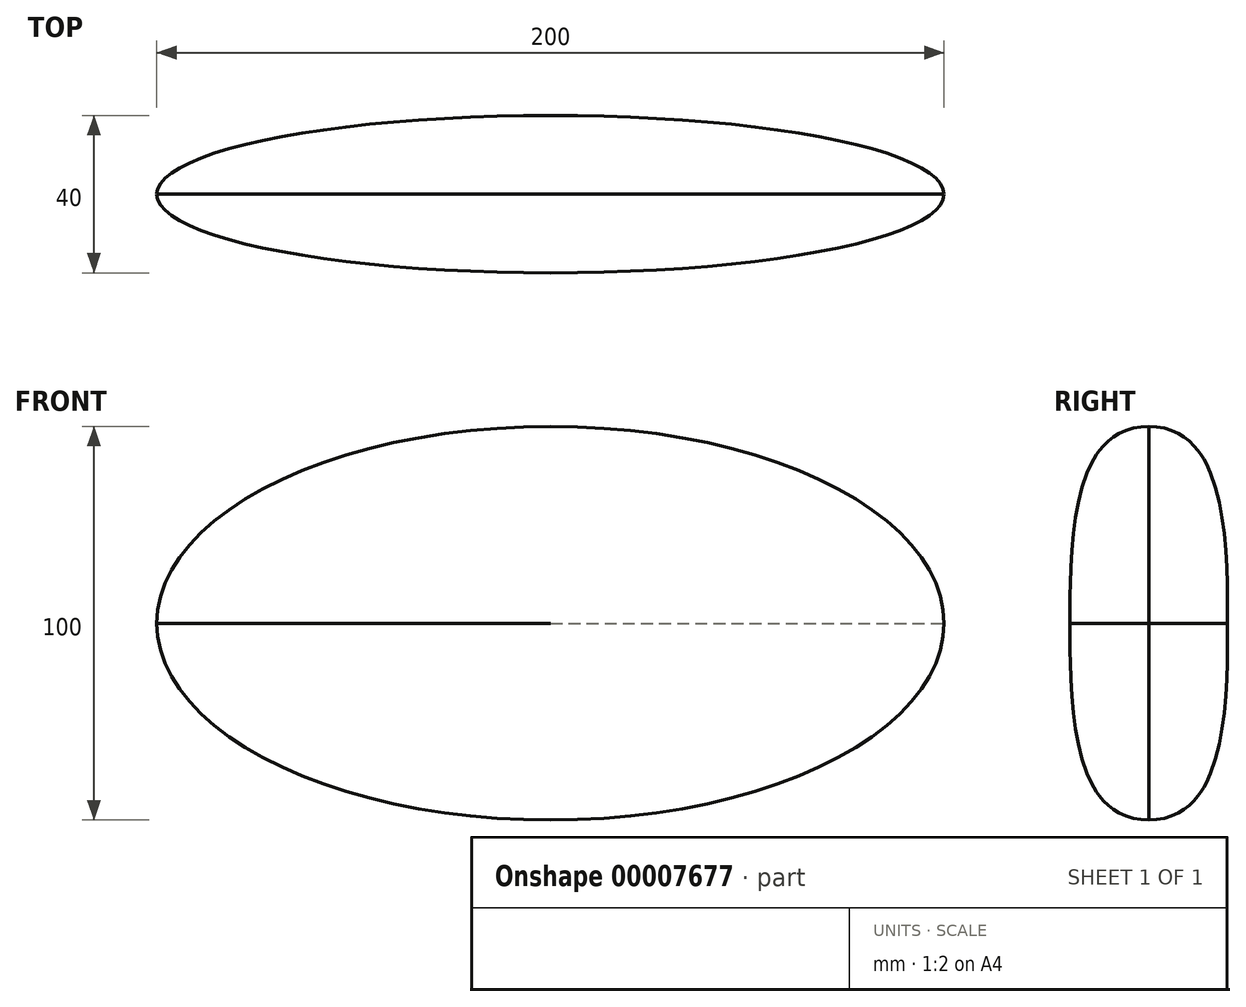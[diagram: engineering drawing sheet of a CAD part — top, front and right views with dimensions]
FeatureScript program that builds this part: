
annotation { "Feature Type Name" : "Feature", "Feature Type Description" : "" }
export const myFeature = defineFeature(function(context is Context, id is Id, definition is map)
    precondition{}
    {
        {
            var Q0;
            Q0=qCreatedBy(makeId("Front.planeOp"),FACE);
            var sketch = newSketch(context, id + "F0", { "sketchPlane" : qUnion([Q0])});
            skLineSegment(sketch, "E0", {"start": v(0, 0) * mm, "end": v(100, 0) * mm, "construction": true});
            skLineSegment(sketch, "E1", {"start": v(0, 0) * mm, "end": v(0, 50) * mm, "construction": true});
            skEllipticalArc(sketch, "E2", {});
            skLineSegment(sketch, "E3", {"start": v(0, 0) * mm, "end": v(-100, 0) * mm, "construction": true});
            const initialGuessF0  = {"E2": [0, 0, 1, 0, 0.1, 0.05, 0, 3.141592653589793]};
            skSetInitialGuess(sketch, initialGuessF0);
            skSolve(sketch);
        }
        {
            var Q0;
            Q0=qCreatedBy(makeId("Top.planeOp"),FACE);
            var sketch = newSketch(context, id + "F1", { "sketchPlane" : qUnion([Q0])});
            skLineSegment(sketch, "E4.0", {"start": v(0, 0) * mm, "end": v(100, 0) * mm});
            skLineSegment(sketch, "E4.1", {"start": v(0, 0) * mm, "end": v(0, 20) * mm});
            skLineSegment(sketch, "E4.3", {"start": v(0, 0) * mm, "end": v(-100, 0) * mm});
            skEllipticalArc(sketch, "E5", {});
            const initialGuessF1  = {"E5": [0, 0, 1, 0, 0.1, 0.02, 0, 3.141592653589793]};
            skSetInitialGuess(sketch, initialGuessF1);
            skSolve(sketch);
        }
        {
            var Q0;
            Q0=qCreatedBy(makeId("Right.planeOp"),FACE);
            var sketch = newSketch(context, id + "F2", { "sketchPlane" : qUnion([Q0])});
            skFitSpline(sketch, "E6", {"points": [v(0, 50) * mm, v(20, 0) * mm], "startDerivative": vector(60, 0) * mm, "endDerivative": vector(0, -60) * mm});
            skLineSegment(sketch, "E7", {"start": v(0, 50) * mm, "end": v(20, 50) * mm});
            skLineSegment(sketch, "E8", {"start": v(20, 0) * mm, "end": v(20, 20) * mm});
            skSolve(sketch);
        }
        {
            var Q0;
            Q0 = qSketchRegion(id + "F0", true);
            var Q1;
            Q1 = qSketchRegion(id + "F1", true);
            var Q2;
            Q2=sQuery(id+"F0.wireOp",EDGE,"E2");
            var Q3;
            Q3=sQuery(id+"F1.wireOp",EDGE,"E5");
            var Q4;
            Q4=sQuery(id+"F2.wireOp",EDGE,"E6");
            loft(context, id + "F3", {"bodyType" : ToolBodyType.SURFACE, "addGuides" : true, "sheetProfilesArray" : [{ "sheetProfileEntities" : qUnion([Q0]) }, { "sheetProfileEntities" : qUnion([Q1]) }], "wireProfilesArray" : [{ "wireProfileEntities" : qUnion([Q2]) }, { "wireProfileEntities" : qUnion([Q3]) }], "guidesArray" : [{ "guideEntities" : qUnion([Q4]), "guideDerivativeType" : LoftGuideDerivativeType.DEFAULT, "guideDerivativeMagnitude" : 1 }]});
        }
        {
            var Q0;
            Q0=makeQuery(id+"F3.opLoft","SWEPT_BODY",BODY,{"disambiguationData":[OSD([sQuery(id+"F0.wireOp",EDGE,"E2"),sQuery(id+"F1.wireOp",EDGE,"E5"),sQuery(id+"F2.wireOp",EDGE,"E6")])]});
            var Q1;
            Q1=qCreatedBy(makeId("Top.planeOp"),FACE);
            mirror(context, id + "F4", {"entities" : qUnion([Q0]), "mirrorPlane" : qUnion([Q1])});
        }
        {
            var Q0;
            Q0=makeQuery(id+"F3.opLoft","SWEPT_BODY",BODY,{"disambiguationData":[OSD([sQuery(id+"F0.wireOp",EDGE,"E2"),sQuery(id+"F1.wireOp",EDGE,"E5"),sQuery(id+"F2.wireOp",EDGE,"E6")])]});
            var Q1;
            Q1=makeQuery(id+"F4.opPattern","COPY",BODY,{"derivedFrom":makeQuery(id+"F3.opLoft","SWEPT_BODY",BODY,{"disambiguationData":[OSD([sQuery(id+"F0.wireOp",EDGE,"E2"),sQuery(id+"F1.wireOp",EDGE,"E5"),sQuery(id+"F2.wireOp",EDGE,"E6")])]}),"instanceName":"1"});
            var Q2;
            Q2=qCreatedBy(makeId("Front.planeOp"),FACE);
            mirror(context, id + "F5", {"entities" : qUnion([Q0, Q1]), "mirrorPlane" : qUnion([Q2])});
        }
    });
